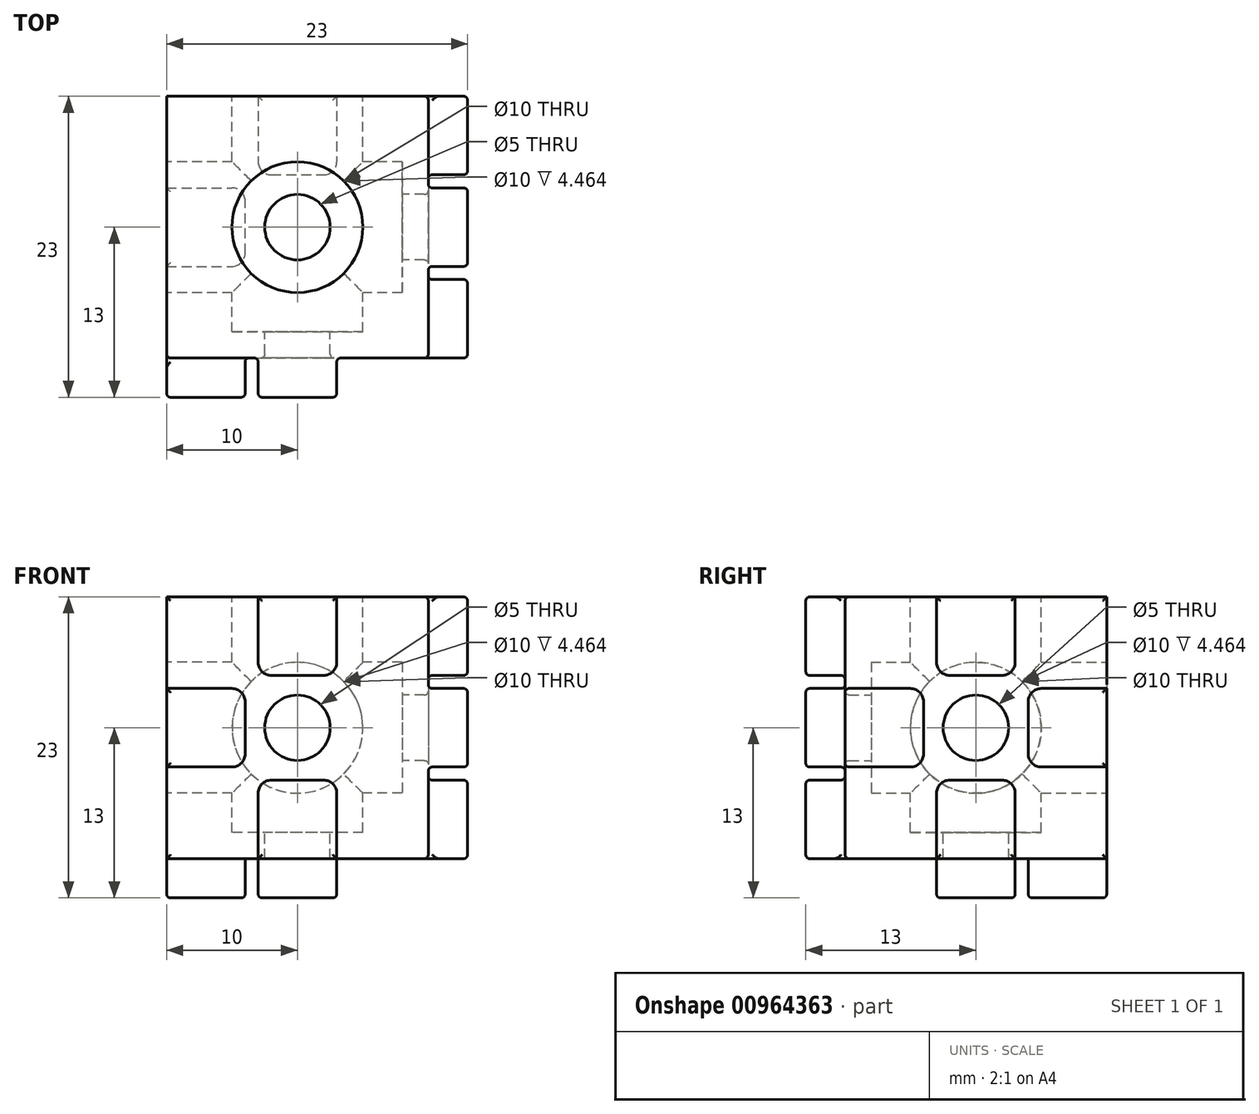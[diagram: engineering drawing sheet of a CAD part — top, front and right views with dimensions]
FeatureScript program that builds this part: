
annotation { "Feature Type Name" : "Feature", "Feature Type Description" : "" }
export const myFeature = defineFeature(function(context is Context, id is Id, definition is map)
    precondition{}
    {
        {
            assignVariable(context, id + "F0", {"name" : "side", "anyValue" : 20 * mm});
        }
        {
            assignVariable(context, id + "F1", {"name" : "leg", "anyValue" : 3 * mm});
        }
        {
            var Q0;
            Q0=qCreatedBy(makeId("Top.planeOp"),FACE);
            var sketch = newSketch(context, id + "F2", { "sketchPlane" : qUnion([Q0])});
            skLineSegment(sketch, "E0.bottom", {"start": v(-20, 0) * mm, "end": v(0, 0) * mm});
            skLineSegment(sketch, "E0.top", {"start": v(-20, -20) * mm, "end": v(0, -20) * mm});
            skLineSegment(sketch, "E0.left", {"start": v(-20, 0) * mm, "end": v(-20, -20) * mm});
            skLineSegment(sketch, "E0.right", {"start": v(0, 0) * mm, "end": v(0, -20) * mm});
            skLineSegment(sketch, "E1", {"start": v(0, 0) * mm, "end": v(-20, -20) * mm, "construction": true});
            skLineSegment(sketch, "E2", {"start": v(-20, 0) * mm, "end": v(0, -20) * mm, "construction": true});
            skCircle(sketch, "E3", {"center": v(-10, -10) * mm, "radius": 2.5 * mm});
            skCircle(sketch, "E4", {"center": v(-10, -10) * mm, "radius": 5 * mm});
            skSolve(sketch);
        }
        {
            var Q0;
            Q0=makeQuery(id+"F2.imprint","IMPRINT",FACE,{"disambiguationData":[TD([[makeQuery(id+"F2.imprint","IMPRINT",EDGE,{"derivedFrom":sQuery(id+"F2.wireOp",EDGE,"E0.bottom")}),-1.0]])]});
            var Q1;
            Q1=makeQuery(id+"F2.imprint","IMPRINT",FACE,{"disambiguationData":[TD([[makeQuery(id+"F2.imprint","IMPRINT",EDGE,{"derivedFrom":sQuery(id+"F2.wireOp",EDGE,"E3")}),-1.0]])]});
            var Q2;
            Q2=makeQuery(id+"F2.imprint","IMPRINT",FACE,{"disambiguationData":[TD([[makeQuery(id+"F2.imprint","IMPRINT",EDGE,{"derivedFrom":sQuery(id+"F2.wireOp",EDGE,"E3")}),1.0]])]});
            extrude(context, id + "F3", {"entities" : qUnion([Q0, Q1, Q2]), "oppositeDirection" : true, "depth" : 20 * mm, "offsetDistance" : 25 * mm});
        }
        {
            var Q0;
            Q0=makeQuery(id+"F2.imprint","IMPRINT",FACE,{"disambiguationData":[TD([[makeQuery(id+"F2.imprint","IMPRINT",EDGE,{"derivedFrom":sQuery(id+"F2.wireOp",EDGE,"E3")}),1.0]])]});
            extrude(context, id + "F4", {"entities" : qUnion([Q0]), "operationType" : NewBodyOperationType.REMOVE, "endBound" : BoundingType.THROUGH_ALL, "oppositeDirection" : true, "depth" : 25 * mm, "offsetDistance" : 25 * mm});
        }
        {
            var Q0;
            Q0=makeQuery(id+"F2.imprint","IMPRINT",FACE,{"disambiguationData":[TD([[makeQuery(id+"F2.imprint","IMPRINT",EDGE,{"derivedFrom":sQuery(id+"F2.wireOp",EDGE,"E3")}),-1.0]])]});
            extrude(context, id + "F5", {"entities" : qUnion([Q0]), "operationType" : NewBodyOperationType.REMOVE, "oppositeDirection" : true, "depth" : 18 * mm, "offsetDistance" : 25 * mm});
        }
        {
            var Q0;
            Q0=makeQuery(id+"F3.opExtrude","SWEPT_FACE",FACE,{"disambiguationData":[OSD([sQuery(id+"F2.wireOp",EDGE,"E0.left")])]});
            var sketch = newSketch(context, id + "F6", { "sketchPlane" : qUnion([Q0])});
            skLineSegment(sketch, "E5", {"start": v(0, 0) * mm, "end": v(20, -20) * mm, "construction": true});
            skLineSegment(sketch, "E6", {"start": v(0, -20) * mm, "end": v(20, 0) * mm, "construction": true});
            skCircle(sketch, "E7", {"center": v(10, -10) * mm, "radius": 2.5 * mm});
            skCircle(sketch, "E8", {"center": v(10, -10) * mm, "radius": 5 * mm});
            skSolve(sketch);
        }
        {
            var Q0;
            Q0=makeQuery(id+"F6.imprint","IMPRINT",FACE,{"disambiguationData":[TD([[makeQuery(id+"F6.imprint","IMPRINT",EDGE,{"derivedFrom":sQuery(id+"F6.wireOp",EDGE,"E7")}),1.0]])]});
            var Q1;
            Q1=makeQuery(id+"F3.opExtrude","SWEPT_FACE",FACE,{"disambiguationData":[OSD([sQuery(id+"F2.wireOp",EDGE,"E0.right")])]});
            extrude(context, id + "F7", {"entities" : qUnion([Q0]), "operationType" : NewBodyOperationType.REMOVE, "endBound" : BoundingType.THROUGH_ALL, "oppositeDirection" : true, "depth" : getVariable(context, 'side'), "endBoundEntityFace" : qUnion([Q1]), "offsetDistance" : 25 * mm});
        }
        {
            var Q0;
            Q0=makeQuery(id+"F6.imprint","IMPRINT",FACE,{"disambiguationData":[TD([[makeQuery(id+"F6.imprint","IMPRINT",EDGE,{"derivedFrom":sQuery(id+"F6.wireOp",EDGE,"E7")}),-1.0]])]});
            extrude(context, id + "F8", {"entities" : qUnion([Q0]), "operationType" : NewBodyOperationType.REMOVE, "oppositeDirection" : true, "depth" : 18 * mm, "offsetDistance" : 25 * mm});
        }
        {
            var Q0;
            Q0=makeQuery(id+"F3.opExtrude","SWEPT_FACE",FACE,{"disambiguationData":[OSD([sQuery(id+"F2.wireOp",EDGE,"E0.bottom")])]});
            var sketch = newSketch(context, id + "F9", { "sketchPlane" : qUnion([Q0])});
            skLineSegment(sketch, "E9", {"start": v(0, 0) * mm, "end": v(20, -20) * mm, "construction": true});
            skLineSegment(sketch, "E10", {"start": v(20, 0) * mm, "end": v(0, -20) * mm, "construction": true});
            skCircle(sketch, "E11", {"center": v(10, -10) * mm, "radius": 5 * mm});
            skCircle(sketch, "E12", {"center": v(10, -10) * mm, "radius": 2.5 * mm});
            skSolve(sketch);
        }
        {
            var Q0;
            Q0=makeQuery(id+"F9.imprint","IMPRINT",FACE,{"disambiguationData":[TD([[makeQuery(id+"F9.imprint","IMPRINT",EDGE,{"derivedFrom":sQuery(id+"F9.wireOp",EDGE,"E12")}),1.0]])]});
            extrude(context, id + "F10", {"entities" : qUnion([Q0]), "operationType" : NewBodyOperationType.REMOVE, "endBound" : BoundingType.THROUGH_ALL, "oppositeDirection" : true, "depth" : 25 * mm, "offsetDistance" : 25 * mm});
        }
        {
            var Q0;
            Q0=makeQuery(id+"F9.imprint","IMPRINT",FACE,{"disambiguationData":[TD([[makeQuery(id+"F9.imprint","IMPRINT",EDGE,{"derivedFrom":sQuery(id+"F9.wireOp",EDGE,"E11")}),1.0]])]});
            extrude(context, id + "F11", {"entities" : qUnion([Q0]), "operationType" : NewBodyOperationType.REMOVE, "oppositeDirection" : true, "depth" : 18 * mm, "offsetDistance" : 25 * mm});
        }
        {
            var Q0;
            Q0=makeQuery(id+"F3.opExtrude","SWEPT_FACE",FACE,{"disambiguationData":[OSD([sQuery(id+"F2.wireOp",EDGE,"E0.right")])]});
            var Q1;
            Q1=makeQuery(id+"F3.opExtrude","SWEPT_FACE",FACE,{"disambiguationData":[OSD([sQuery(id+"F2.wireOp",EDGE,"E0.right")])]});
            var sketch = newSketch(context, id + "F12", { "sketchPlane" : qUnion([Q0, Q1])});
            skLineSegment(sketch, "E13.0.0", {"start": v(0, 0) * mm, "end": v(-20, 0) * mm, "construction": true});
            skLineSegment(sketch, "E13.0.2", {"start": v(-20, -20) * mm, "end": v(0, -20) * mm, "construction": true});
            skLineSegment(sketch, "E13.0.3", {"start": v(0, -20) * mm, "end": v(0, 0) * mm, "construction": true});
            skLineSegment(sketch, "E14", {"start": v(-20, -10) * mm, "end": v(0, -10) * mm, "construction": true});
            skLineSegment(sketch, "E15", {"start": v(-10, 0) * mm, "end": v(-10, -20) * mm, "construction": true});
            skLineSegment(sketch, "E16.bottom", {"start": v(-20, -7) * mm, "end": v(-15, -7) * mm});
            skLineSegment(sketch, "E16.top", {"start": v(-20, -13) * mm, "end": v(-15, -13) * mm});
            skLineSegment(sketch, "E16.left", {"start": v(-20, -7) * mm, "end": v(-20, -13) * mm});
            skLineSegment(sketch, "E16.right", {"start": v(-14, -8) * mm, "end": v(-14, -12) * mm});
            skPoint(sketch, "E17", {"position": v(-14, -10) * mm});
            skPoint(sketch, "E18", {"position": v(-10, -10) * mm});
            skLineSegment(sketch, "E19.1.0", {"start": v(-13, -20) * mm, "end": v(-13, -15) * mm});
            skLineSegment(sketch, "E19.1.1", {"start": v(-13, -20) * mm, "end": v(-7, -20) * mm});
            skLineSegment(sketch, "E19.1.2", {"start": v(-7, -20) * mm, "end": v(-7, -15) * mm});
            skLineSegment(sketch, "E19.1.3", {"start": v(-12, -14) * mm, "end": v(-8, -14) * mm});
            skLineSegment(sketch, "E19.2.0", {"start": v(0, -13) * mm, "end": v(-5, -13) * mm});
            skLineSegment(sketch, "E19.2.1", {"start": v(0, -13) * mm, "end": v(0, -7) * mm});
            skLineSegment(sketch, "E19.2.2", {"start": v(0, -7) * mm, "end": v(-5, -7) * mm});
            skLineSegment(sketch, "E19.2.3", {"start": v(-6, -12) * mm, "end": v(-6, -8) * mm});
            skLineSegment(sketch, "E20.1.3.0", {"start": v(-7, 0) * mm, "end": v(-7, -5) * mm});
            skLineSegment(sketch, "E20.3.3.0", {"start": v(-7, 0) * mm, "end": v(-13, 0) * mm});
            skLineSegment(sketch, "E20.6.3.0", {"start": v(-13, 0) * mm, "end": v(-13, -5) * mm});
            skLineSegment(sketch, "E20.9.3.0", {"start": v(-8, -6) * mm, "end": v(-12, -6) * mm});
            skPoint(sketch, "E21.visualSharp", {"position": v(-13, -6) * mm});
            skArc(sketch, "E21.filletArc", {"start": v(-13, -5) * mm, "mid": v(-12.7, -5.7) * mm, "end": v(-12, -6) * mm});
            skPoint(sketch, "E22.visualSharp", {"position": v(-7, -6) * mm});
            skArc(sketch, "E22.filletArc", {"start": v(-8, -6) * mm, "mid": v(-7.3, -5.7) * mm, "end": v(-7, -5) * mm});
            skPoint(sketch, "E23.visualSharp", {"position": v(-6, -7) * mm});
            skArc(sketch, "E23.filletArc", {"start": v(-5, -7) * mm, "mid": v(-5.7, -7.3) * mm, "end": v(-6, -8) * mm});
            skPoint(sketch, "E24.visualSharp", {"position": v(-14, -7) * mm});
            skArc(sketch, "E24.filletArc", {"start": v(-14, -8) * mm, "mid": v(-14.3, -7.3) * mm, "end": v(-15, -7) * mm});
            skPoint(sketch, "E25.visualSharp", {"position": v(-14, -13) * mm});
            skArc(sketch, "E25.filletArc", {"start": v(-15, -13) * mm, "mid": v(-14.3, -12.7) * mm, "end": v(-14, -12) * mm});
            skPoint(sketch, "E26.visualSharp", {"position": v(-6, -13) * mm});
            skArc(sketch, "E26.filletArc", {"start": v(-6, -12) * mm, "mid": v(-5.7, -12.7) * mm, "end": v(-5, -13) * mm});
            skPoint(sketch, "E27.visualSharp", {"position": v(-7, -14) * mm});
            skArc(sketch, "E27.filletArc", {"start": v(-7, -15) * mm, "mid": v(-7.3, -14.3) * mm, "end": v(-8, -14) * mm});
            skPoint(sketch, "E28.visualSharp", {"position": v(-13, -14) * mm});
            skArc(sketch, "E28.filletArc", {"start": v(-12, -14) * mm, "mid": v(-12.7, -14.3) * mm, "end": v(-13, -15) * mm});
            skSolve(sketch);
        }
        {
            var Q0;
            Q0=makeQuery(id+"F12.imprint","IMPRINT",FACE,{"disambiguationData":[TD([[makeQuery(id+"F12.imprint","IMPRINT",EDGE,{"derivedFrom":sQuery(id+"F12.wireOp",EDGE,"E20.1.3.0")}),-1.0]])]});
            var Q1;
            Q1=makeQuery(id+"F12.imprint","IMPRINT",FACE,{"disambiguationData":[TD([[makeQuery(id+"F12.imprint","IMPRINT",EDGE,{"derivedFrom":sQuery(id+"F12.wireOp",EDGE,"E16.bottom")}),-1.0]])]});
            var Q2;
            Q2=makeQuery(id+"F12.imprint","IMPRINT",FACE,{"disambiguationData":[TD([[makeQuery(id+"F12.imprint","IMPRINT",EDGE,{"derivedFrom":sQuery(id+"F12.wireOp",EDGE,"E19.2.0")}),-1.0]])]});
            var Q3;
            Q3=makeQuery(id+"F12.imprint","IMPRINT",FACE,{"disambiguationData":[TD([[makeQuery(id+"F12.imprint","IMPRINT",EDGE,{"derivedFrom":sQuery(id+"F12.wireOp",EDGE,"E19.1.0")}),-1.0]])]});
            extrude(context, id + "F13", {"entities" : qUnion([Q0, Q1, Q2, Q3]), "operationType" : NewBodyOperationType.ADD, "depth" : getVariable(context, 'leg'), "offsetDistance" : 25 * mm});
        }
        {
            var Q0;
            Q0=makeQuery(id+"F3.opExtrude","SWEPT_FACE",FACE,{"disambiguationData":[OSD([sQuery(id+"F2.wireOp",EDGE,"E0.right")])]});
            var Q1;
            Q1=makeQuery(id+"F13.opExtrude","CAP_FACE",FACE,{"disambiguationData":[OSD([sQuery(id+"F12.wireOp",EDGE,"E20.1.3.0"),sQuery(id+"F12.wireOp",EDGE,"E20.3.3.0"),sQuery(id+"F12.wireOp",EDGE,"E20.6.3.0"),sQuery(id+"F12.wireOp",EDGE,"E20.9.3.0"),sQuery(id+"F12.wireOp",EDGE,"E21.filletArc"),sQuery(id+"F12.wireOp",EDGE,"E22.filletArc")])],"isStart":false});
            var Q2;
            Q2=makeQuery(id+"F13.opExtrude","CAP_FACE",FACE,{"disambiguationData":[OSD([sQuery(id+"F12.wireOp",EDGE,"E19.2.0"),sQuery(id+"F12.wireOp",EDGE,"E19.2.1"),sQuery(id+"F12.wireOp",EDGE,"E19.2.2"),sQuery(id+"F12.wireOp",EDGE,"E19.2.3"),sQuery(id+"F12.wireOp",EDGE,"E23.filletArc"),sQuery(id+"F12.wireOp",EDGE,"E26.filletArc")])],"isStart":false});
            var Q3;
            Q3=makeQuery(id+"F13.opExtrude","CAP_FACE",FACE,{"disambiguationData":[OSD([sQuery(id+"F12.wireOp",EDGE,"E16.bottom"),sQuery(id+"F12.wireOp",EDGE,"E16.top"),sQuery(id+"F12.wireOp",EDGE,"E16.left"),sQuery(id+"F12.wireOp",EDGE,"E16.right"),sQuery(id+"F12.wireOp",EDGE,"E24.filletArc"),sQuery(id+"F12.wireOp",EDGE,"E25.filletArc")])],"isStart":false});
            var Q4;
            Q4=makeQuery(id+"F13.opExtrude","CAP_FACE",FACE,{"disambiguationData":[OSD([sQuery(id+"F12.wireOp",EDGE,"E19.1.0"),sQuery(id+"F12.wireOp",EDGE,"E19.1.1"),sQuery(id+"F12.wireOp",EDGE,"E19.1.2"),sQuery(id+"F12.wireOp",EDGE,"E19.1.3"),sQuery(id+"F12.wireOp",EDGE,"E27.filletArc"),sQuery(id+"F12.wireOp",EDGE,"E28.filletArc")])],"isStart":false});
            fillet(context, id + "F14", {"entities" : qUnion([Q0, Q1, Q2, Q3, Q4]), "radius" : .3 * mm, "tangentPropagation" : true, "allowEdgeOverflow" : false});
        }
        {
            var Q0;
            Q0=makeQuery(id+"F13.boolean.opBoolean","MERGE",FACE,{"derivedFrom":[makeQuery(id+"F3.opExtrude","SWEPT_FACE",FACE,{"disambiguationData":[OSD([sQuery(id+"F2.wireOp",EDGE,"E0.top")])]}),makeQuery(id+"F13.opExtrude","SWEPT_FACE",FACE,{"disambiguationData":[OSD([sQuery(id+"F12.wireOp",EDGE,"E16.left")])]})]});
            var sketch = newSketch(context, id + "F15", { "sketchPlane" : qUnion([Q0])});
            skLineSegment(sketch, "E29.0.0", {"start": v(0, 0) * mm, "end": v(-20, 0) * mm, "construction": true});
            skLineSegment(sketch, "E29.0.2", {"start": v(-20, -20) * mm, "end": v(0, -20) * mm, "construction": true});
            skLineSegment(sketch, "E29.0.3", {"start": v(0, -20) * mm, "end": v(0, 0) * mm, "construction": true});
            skLineSegment(sketch, "E30", {"start": v(-20, -10) * mm, "end": v(0, -10) * mm, "construction": true});
            skLineSegment(sketch, "E31", {"start": v(-10, 0) * mm, "end": v(-10, -20) * mm, "construction": true});
            skLineSegment(sketch, "E32.bottom", {"start": v(-20, -7) * mm, "end": v(-15, -7) * mm});
            skLineSegment(sketch, "E32.top", {"start": v(-20, -13) * mm, "end": v(-15, -13) * mm});
            skLineSegment(sketch, "E32.left", {"start": v(-20, -7) * mm, "end": v(-20, -13) * mm});
            skLineSegment(sketch, "E32.right", {"start": v(-14, -8) * mm, "end": v(-14, -12) * mm});
            skPoint(sketch, "E33", {"position": v(-14, -10) * mm});
            skPoint(sketch, "E34", {"position": v(-10, -10) * mm});
            skLineSegment(sketch, "E35.1.0", {"start": v(-13, -20) * mm, "end": v(-13, -15) * mm});
            skLineSegment(sketch, "E35.1.1", {"start": v(-13, -20) * mm, "end": v(-7, -20) * mm});
            skLineSegment(sketch, "E35.1.2", {"start": v(-7, -20) * mm, "end": v(-7, -15) * mm});
            skLineSegment(sketch, "E35.1.3", {"start": v(-12, -14) * mm, "end": v(-8, -14) * mm});
            skLineSegment(sketch, "E35.2.0", {"start": v(0, -13) * mm, "end": v(-5, -13) * mm});
            skLineSegment(sketch, "E35.2.1", {"start": v(0, -13) * mm, "end": v(0, -7) * mm});
            skLineSegment(sketch, "E35.2.2", {"start": v(0, -7) * mm, "end": v(-5, -7) * mm});
            skLineSegment(sketch, "E35.2.3", {"start": v(-6, -12) * mm, "end": v(-6, -8) * mm});
            skLineSegment(sketch, "E36.1.3.0", {"start": v(-7, 0) * mm, "end": v(-7, -5) * mm});
            skLineSegment(sketch, "E36.3.3.0", {"start": v(-7, 0) * mm, "end": v(-13, 0) * mm});
            skLineSegment(sketch, "E36.6.3.0", {"start": v(-13, 0) * mm, "end": v(-13, -5) * mm});
            skLineSegment(sketch, "E36.9.3.0", {"start": v(-8, -6) * mm, "end": v(-12, -6) * mm});
            skPoint(sketch, "E37.visualSharp", {"position": v(-13, -6) * mm});
            skArc(sketch, "E37.filletArc", {"start": v(-13, -5) * mm, "mid": v(-12.7, -5.7) * mm, "end": v(-12, -6) * mm});
            skPoint(sketch, "E38.visualSharp", {"position": v(-7, -6) * mm});
            skArc(sketch, "E38.filletArc", {"start": v(-8, -6) * mm, "mid": v(-7.3, -5.7) * mm, "end": v(-7, -5) * mm});
            skPoint(sketch, "E39.visualSharp", {"position": v(-6, -7) * mm});
            skArc(sketch, "E39.filletArc", {"start": v(-5, -7) * mm, "mid": v(-5.7, -7.3) * mm, "end": v(-6, -8) * mm});
            skPoint(sketch, "E40.visualSharp", {"position": v(-14, -7) * mm});
            skArc(sketch, "E40.filletArc", {"start": v(-14, -8) * mm, "mid": v(-14.3, -7.3) * mm, "end": v(-15, -7) * mm});
            skPoint(sketch, "E41.visualSharp", {"position": v(-14, -13) * mm});
            skArc(sketch, "E41.filletArc", {"start": v(-15, -13) * mm, "mid": v(-14.3, -12.7) * mm, "end": v(-14, -12) * mm});
            skPoint(sketch, "E42.visualSharp", {"position": v(-6, -13) * mm});
            skArc(sketch, "E42.filletArc", {"start": v(-6, -12) * mm, "mid": v(-5.7, -12.7) * mm, "end": v(-5, -13) * mm});
            skPoint(sketch, "E43.visualSharp", {"position": v(-7, -14) * mm});
            skArc(sketch, "E43.filletArc", {"start": v(-7, -15) * mm, "mid": v(-7.3, -14.3) * mm, "end": v(-8, -14) * mm});
            skPoint(sketch, "E44.visualSharp", {"position": v(-13, -14) * mm});
            skArc(sketch, "E44.filletArc", {"start": v(-12, -14) * mm, "mid": v(-12.7, -14.3) * mm, "end": v(-13, -15) * mm});
            skSolve(sketch);
        }
        {
            var Q0;
            Q0=makeQuery(id+"F15.imprint","IMPRINT",FACE,{"disambiguationData":[TD([[makeQuery(id+"F15.imprint","IMPRINT",EDGE,{"derivedFrom":sQuery(id+"F15.wireOp",EDGE,"E36.1.3.0")}),-1.0]])]});
            var Q1;
            Q1=makeQuery(id+"F15.imprint","IMPRINT",FACE,{"disambiguationData":[TD([[makeQuery(id+"F15.imprint","IMPRINT",EDGE,{"derivedFrom":sQuery(id+"F15.wireOp",EDGE,"E32.bottom")}),-1.0]])]});
            var Q2;
            Q2=makeQuery(id+"F15.imprint","IMPRINT",FACE,{"disambiguationData":[TD([[makeQuery(id+"F15.imprint","IMPRINT",EDGE,{"derivedFrom":sQuery(id+"F15.wireOp",EDGE,"E35.2.3")}),-1.0]])]});
            var Q3;
            Q3=makeQuery(id+"F15.imprint","IMPRINT",FACE,{"disambiguationData":[TD([[makeQuery(id+"F15.imprint","IMPRINT",EDGE,{"derivedFrom":sQuery(id+"F15.wireOp",EDGE,"E35.1.0")}),-1.0]])]});
            extrude(context, id + "F16", {"entities" : qUnion([Q0, Q1, Q2, Q3]), "operationType" : NewBodyOperationType.ADD, "depth" : getVariable(context, 'leg'), "offsetDistance" : 25 * mm});
        }
        {
            var Q0;
            {var subQ1=sQuery(id+"F2.wireOp",EDGE,"E0.left");var subQ2=sQuery(id+"F2.wireOp",EDGE,"E0.top");var subQ6=sQuery(id+"F12.wireOp",EDGE,"E16.left");var subQ7=makeQuery(id+"F13.opExtrude","SWEPT_FACE",FACE,{"disambiguationData":[OSD([subQ6])]});var subQ8=makeQuery(id+"F3.opExtrude","SWEPT_FACE",FACE,{"disambiguationData":[OSD([subQ2])]});var subQ12=makeQuery(id+"F3.opExtrude","SWEPT_FACE",FACE,{"disambiguationData":[OSD([subQ1])]});Q0=makeQuery(id+"F16.boolean.opBoolean","SPLIT",FACE,{"disambiguationData":[TD([subQ12])],"derivedFrom":makeQuery(id+"F13.boolean.opBoolean","MERGE",FACE,{"derivedFrom":[subQ8,subQ7]})});}
            var Q1;
            Q1=makeQuery(id+"F16.opExtrude","CAP_FACE",FACE,{"disambiguationData":[OSD([sQuery(id+"F15.wireOp",EDGE,"E32.bottom"),sQuery(id+"F15.wireOp",EDGE,"E32.top"),sQuery(id+"F15.wireOp",EDGE,"E32.left"),sQuery(id+"F15.wireOp",EDGE,"E32.right"),sQuery(id+"F15.wireOp",EDGE,"E40.filletArc"),sQuery(id+"F15.wireOp",EDGE,"E41.filletArc")])],"isStart":false});
            var Q2;
            Q2=makeQuery(id+"F16.opExtrude","CAP_FACE",FACE,{"disambiguationData":[OSD([sQuery(id+"F15.wireOp",EDGE,"E36.1.3.0"),sQuery(id+"F15.wireOp",EDGE,"E36.3.3.0"),sQuery(id+"F15.wireOp",EDGE,"E36.6.3.0"),sQuery(id+"F15.wireOp",EDGE,"E36.9.3.0"),sQuery(id+"F15.wireOp",EDGE,"E37.filletArc"),sQuery(id+"F15.wireOp",EDGE,"E38.filletArc")])],"isStart":false});
            var Q3;
            Q3=makeQuery(id+"F16.opExtrude","CAP_FACE",FACE,{"disambiguationData":[OSD([sQuery(id+"F2.wireOp",EDGE,"E0.top"),sQuery(id+"F2.wireOp",EDGE,"E0.right"),sQuery(id+"F12.wireOp",EDGE,"E16.bottom"),sQuery(id+"F12.wireOp",EDGE,"E16.top"),sQuery(id+"F12.wireOp",EDGE,"E16.left"),sQuery(id+"F15.wireOp",EDGE,"E35.2.0"),sQuery(id+"F15.wireOp",EDGE,"E35.2.1"),sQuery(id+"F15.wireOp",EDGE,"E35.2.2"),sQuery(id+"F15.wireOp",EDGE,"E35.2.3"),sQuery(id+"F15.wireOp",EDGE,"E39.filletArc"),sQuery(id+"F15.wireOp",EDGE,"E42.filletArc")])],"isStart":false});
            var Q4;
            Q4=makeQuery(id+"F16.opExtrude","CAP_FACE",FACE,{"disambiguationData":[OSD([sQuery(id+"F15.wireOp",EDGE,"E35.1.0"),sQuery(id+"F15.wireOp",EDGE,"E35.1.1"),sQuery(id+"F15.wireOp",EDGE,"E35.1.2"),sQuery(id+"F15.wireOp",EDGE,"E35.1.3"),sQuery(id+"F15.wireOp",EDGE,"E43.filletArc"),sQuery(id+"F15.wireOp",EDGE,"E44.filletArc")])],"isStart":false});
            fillet(context, id + "F17", {"entities" : qUnion([Q0, Q1, Q2, Q3, Q4]), "radius" : .3 * mm, "tangentPropagation" : true, "allowEdgeOverflow" : false});
        }
        {
            var Q0;
            Q0=makeQuery(id+"F16.boolean.opBoolean","MERGE",FACE,{"derivedFrom":[makeQuery(id+"F13.boolean.opBoolean","MERGE",FACE,{"derivedFrom":[makeQuery(id+"F3.opExtrude","CAP_FACE",FACE,{"disambiguationData":[OSD([sQuery(id+"F2.wireOp",EDGE,"E0.bottom"),sQuery(id+"F2.wireOp",EDGE,"E0.top"),sQuery(id+"F2.wireOp",EDGE,"E0.left"),sQuery(id+"F2.wireOp",EDGE,"E0.right")])],"isStart":false}),makeQuery(id+"F13.opExtrude","SWEPT_FACE",FACE,{"disambiguationData":[OSD([sQuery(id+"F12.wireOp",EDGE,"E19.1.1")])]})]}),makeQuery(id+"F16.opExtrude","SWEPT_FACE",FACE,{"disambiguationData":[OSD([sQuery(id+"F15.wireOp",EDGE,"E35.1.1")])]})]});
            var sketch = newSketch(context, id + "F18", { "sketchPlane" : qUnion([Q0])});
            skLineSegment(sketch, "E45.0.0", {"start": v(0, 20) * mm, "end": v(-20, 20) * mm, "construction": true});
            skLineSegment(sketch, "E45.0.2", {"start": v(-20, 0) * mm, "end": v(0, 0) * mm, "construction": true});
            skLineSegment(sketch, "E45.0.3", {"start": v(0, 0) * mm, "end": v(0, 20) * mm, "construction": true});
            skLineSegment(sketch, "E46", {"start": v(-20, 10) * mm, "end": v(0, 10) * mm, "construction": true});
            skLineSegment(sketch, "E47", {"start": v(-10, 20) * mm, "end": v(-10, 0) * mm, "construction": true});
            skLineSegment(sketch, "E48.bottom", {"start": v(-20, 13) * mm, "end": v(-15, 13) * mm});
            skLineSegment(sketch, "E48.top", {"start": v(-20, 7) * mm, "end": v(-15, 7) * mm});
            skLineSegment(sketch, "E48.left", {"start": v(-20, 13) * mm, "end": v(-20, 7) * mm});
            skLineSegment(sketch, "E48.right", {"start": v(-14, 12) * mm, "end": v(-14, 8) * mm});
            skPoint(sketch, "E49", {"position": v(-14, 10) * mm});
            skPoint(sketch, "E50", {"position": v(-10, 10) * mm});
            skLineSegment(sketch, "E51.1.0", {"start": v(-13, 0) * mm, "end": v(-13, 5) * mm});
            skLineSegment(sketch, "E51.1.1", {"start": v(-13, 0) * mm, "end": v(-7, 0) * mm});
            skLineSegment(sketch, "E51.1.2", {"start": v(-7, 0) * mm, "end": v(-7, 5) * mm});
            skLineSegment(sketch, "E51.1.3", {"start": v(-12, 6) * mm, "end": v(-8, 6) * mm});
            skLineSegment(sketch, "E51.2.0", {"start": v(0, 7) * mm, "end": v(-5, 7) * mm});
            skLineSegment(sketch, "E51.2.1", {"start": v(0, 7) * mm, "end": v(0, 13) * mm});
            skLineSegment(sketch, "E51.2.2", {"start": v(0, 13) * mm, "end": v(-5, 13) * mm});
            skLineSegment(sketch, "E51.2.3", {"start": v(-6, 8) * mm, "end": v(-6, 12) * mm});
            skLineSegment(sketch, "E52.1.3.0", {"start": v(-7, 20) * mm, "end": v(-7, 15) * mm});
            skLineSegment(sketch, "E52.3.3.0", {"start": v(-7, 20) * mm, "end": v(-13, 20) * mm});
            skLineSegment(sketch, "E52.6.3.0", {"start": v(-13, 20) * mm, "end": v(-13, 15) * mm});
            skLineSegment(sketch, "E52.9.3.0", {"start": v(-8, 14) * mm, "end": v(-12, 14) * mm});
            skPoint(sketch, "E53.visualSharp", {"position": v(-13, 14) * mm});
            skArc(sketch, "E53.filletArc", {"start": v(-13, 15) * mm, "mid": v(-12.7, 14.3) * mm, "end": v(-12, 14) * mm});
            skPoint(sketch, "E54.visualSharp", {"position": v(-7, 14) * mm});
            skArc(sketch, "E54.filletArc", {"start": v(-8, 14) * mm, "mid": v(-7.3, 14.3) * mm, "end": v(-7, 15) * mm});
            skPoint(sketch, "E55.visualSharp", {"position": v(-6, 13) * mm});
            skArc(sketch, "E55.filletArc", {"start": v(-5, 13) * mm, "mid": v(-5.7, 12.7) * mm, "end": v(-6, 12) * mm});
            skPoint(sketch, "E56.visualSharp", {"position": v(-14, 13) * mm});
            skArc(sketch, "E56.filletArc", {"start": v(-14, 12) * mm, "mid": v(-14.3, 12.7) * mm, "end": v(-15, 13) * mm});
            skPoint(sketch, "E57.visualSharp", {"position": v(-14, 7) * mm});
            skArc(sketch, "E57.filletArc", {"start": v(-15, 7) * mm, "mid": v(-14.3, 7.3) * mm, "end": v(-14, 8) * mm});
            skPoint(sketch, "E58.visualSharp", {"position": v(-6, 7) * mm});
            skArc(sketch, "E58.filletArc", {"start": v(-6, 8) * mm, "mid": v(-5.7, 7.3) * mm, "end": v(-5, 7) * mm});
            skPoint(sketch, "E59.visualSharp", {"position": v(-7, 6) * mm});
            skArc(sketch, "E59.filletArc", {"start": v(-7, 5) * mm, "mid": v(-7.3, 5.7) * mm, "end": v(-8, 6) * mm});
            skPoint(sketch, "E60.visualSharp", {"position": v(-13, 6) * mm});
            skArc(sketch, "E60.filletArc", {"start": v(-12, 6) * mm, "mid": v(-12.7, 5.7) * mm, "end": v(-13, 5) * mm});
            skSolve(sketch);
        }
        {
            var Q0;
            Q0=makeQuery(id+"F18.imprint","IMPRINT",FACE,{"disambiguationData":[TD([[makeQuery(id+"F18.imprint","IMPRINT",EDGE,{"derivedFrom":sQuery(id+"F18.wireOp",EDGE,"E52.9.3.0")}),-1.0]])]});
            var Q1;
            Q1=makeQuery(id+"F18.imprint","IMPRINT",FACE,{"disambiguationData":[TD([[makeQuery(id+"F18.imprint","IMPRINT",EDGE,{"derivedFrom":sQuery(id+"F18.wireOp",EDGE,"E48.bottom")}),-1.0]])]});
            var Q2;
            Q2=makeQuery(id+"F18.imprint","IMPRINT",FACE,{"disambiguationData":[TD([[makeQuery(id+"F18.imprint","IMPRINT",EDGE,{"derivedFrom":sQuery(id+"F18.wireOp",EDGE,"E51.2.3")}),-1.0]])]});
            var Q3;
            Q3=makeQuery(id+"F18.imprint","IMPRINT",FACE,{"disambiguationData":[TD([[makeQuery(id+"F18.imprint","IMPRINT",EDGE,{"derivedFrom":sQuery(id+"F18.wireOp",EDGE,"E51.1.0")}),-1.0]])]});
            extrude(context, id + "F19", {"entities" : qUnion([Q0, Q1, Q2, Q3]), "operationType" : NewBodyOperationType.ADD, "depth" : getVariable(context, 'leg'), "offsetDistance" : 25 * mm});
        }
        {
            var Q0;
            Q0=makeQuery(id+"F19.opExtrude","CAP_FACE",FACE,{"disambiguationData":[OSD([sQuery(id+"F2.wireOp",EDGE,"E0.bottom"),sQuery(id+"F2.wireOp",EDGE,"E0.top"),sQuery(id+"F2.wireOp",EDGE,"E0.left"),sQuery(id+"F2.wireOp",EDGE,"E0.right"),sQuery(id+"F12.wireOp",EDGE,"E19.1.1"),sQuery(id+"F15.wireOp",EDGE,"E35.1.0"),sQuery(id+"F15.wireOp",EDGE,"E35.1.1"),sQuery(id+"F15.wireOp",EDGE,"E35.1.2"),sQuery(id+"F18.wireOp",EDGE,"E52.1.3.0"),sQuery(id+"F18.wireOp",EDGE,"E52.3.3.0"),sQuery(id+"F18.wireOp",EDGE,"E52.6.3.0"),sQuery(id+"F18.wireOp",EDGE,"E52.9.3.0"),sQuery(id+"F18.wireOp",EDGE,"E53.filletArc"),sQuery(id+"F18.wireOp",EDGE,"E54.filletArc")])],"isStart":false});
            var Q1;
            Q1=makeQuery(id+"F19.opExtrude","CAP_FACE",FACE,{"disambiguationData":[OSD([sQuery(id+"F2.wireOp",EDGE,"E0.bottom"),sQuery(id+"F2.wireOp",EDGE,"E0.top"),sQuery(id+"F2.wireOp",EDGE,"E0.left"),sQuery(id+"F2.wireOp",EDGE,"E0.right"),sQuery(id+"F12.wireOp",EDGE,"E19.1.0"),sQuery(id+"F12.wireOp",EDGE,"E19.1.1"),sQuery(id+"F12.wireOp",EDGE,"E19.1.2"),sQuery(id+"F18.wireOp",EDGE,"E51.2.0"),sQuery(id+"F18.wireOp",EDGE,"E51.2.1"),sQuery(id+"F18.wireOp",EDGE,"E51.2.2"),sQuery(id+"F18.wireOp",EDGE,"E51.2.3"),sQuery(id+"F18.wireOp",EDGE,"E55.filletArc"),sQuery(id+"F18.wireOp",EDGE,"E58.filletArc")])],"isStart":false});
            var Q2;
            Q2=makeQuery(id+"F19.opExtrude","CAP_FACE",FACE,{"disambiguationData":[OSD([sQuery(id+"F18.wireOp",EDGE,"E51.1.0"),sQuery(id+"F18.wireOp",EDGE,"E51.1.1"),sQuery(id+"F18.wireOp",EDGE,"E51.1.2"),sQuery(id+"F18.wireOp",EDGE,"E51.1.3"),sQuery(id+"F18.wireOp",EDGE,"E59.filletArc"),sQuery(id+"F18.wireOp",EDGE,"E60.filletArc")])],"isStart":false});
            var Q3;
            Q3=makeQuery(id+"F19.opExtrude","CAP_FACE",FACE,{"disambiguationData":[OSD([sQuery(id+"F18.wireOp",EDGE,"E48.bottom"),sQuery(id+"F18.wireOp",EDGE,"E48.top"),sQuery(id+"F18.wireOp",EDGE,"E48.left"),sQuery(id+"F18.wireOp",EDGE,"E48.right"),sQuery(id+"F18.wireOp",EDGE,"E56.filletArc"),sQuery(id+"F18.wireOp",EDGE,"E57.filletArc")])],"isStart":false});
            fillet(context, id + "F20", {"entities" : qUnion([Q0, Q1, Q2, Q3]), "radius" : .3 * mm, "tangentPropagation" : true, "allowEdgeOverflow" : false});
        }
    });
